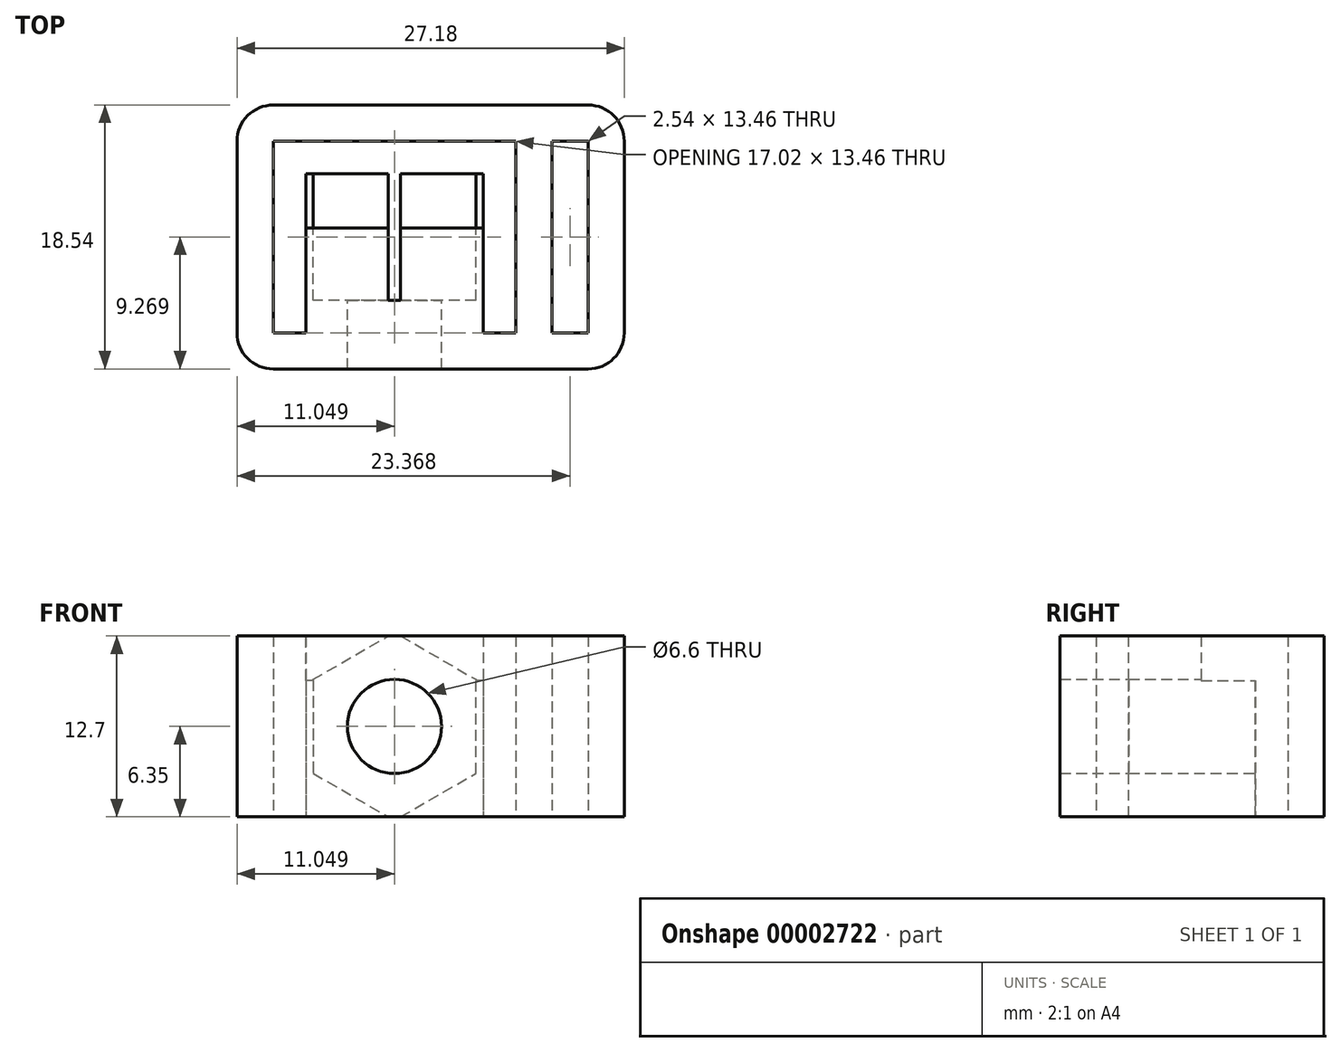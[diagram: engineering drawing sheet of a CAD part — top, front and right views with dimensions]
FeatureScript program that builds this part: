
annotation { "Feature Type Name" : "Feature", "Feature Type Description" : "" }
export const myFeature = defineFeature(function(context is Context, id is Id, definition is map)
    precondition{}
    {
        {
            var Q0;
            Q0=qCreatedBy(makeId("Top.planeOp"),FACE);
            var sketch = newSketch(context, id + "F0", { "sketchPlane" : qUnion([Q0])});
            skLineSegment(sketch, "E0", {"start": v(0, 0) * mm, "end": v(17.02, 0) * mm});
            skLineSegment(sketch, "E1", {"start": v(17.02, 0) * mm, "end": v(17.02, -13.46) * mm});
            skLineSegment(sketch, "E2", {"start": v(17.02, -13.46) * mm, "end": v(14.73, -13.46) * mm});
            skLineSegment(sketch, "E3", {"start": v(14.73, -13.46) * mm, "end": v(14.73, -2.29) * mm});
            skLineSegment(sketch, "E4", {"start": v(14.73, -2.29) * mm, "end": v(2.29, -2.29) * mm});
            skLineSegment(sketch, "E5", {"start": v(2.29, -2.29) * mm, "end": v(2.29, -13.46) * mm});
            skLineSegment(sketch, "E6", {"start": v(2.29, -13.46) * mm, "end": v(0, -13.46) * mm});
            skLineSegment(sketch, "E7", {"start": v(0, -13.46) * mm, "end": v(0, 0) * mm});
            skSolve(sketch);
        }
        {
            var Q0;
            Q0=qCreatedBy(makeId("Top.planeOp"),FACE);
            var sketch = newSketch(context, id + "F1", { "sketchPlane" : qUnion([Q0])});
            skLineSegment(sketch, "E8.0", {"start": v(0, 2.54) * mm, "end": v(17.02, 2.54) * mm});
            skLineSegment(sketch, "E9.0", {"start": v(-2.54, -13.46) * mm, "end": v(-2.54, 0) * mm});
            skLineSegment(sketch, "E10.0", {"start": v(19.56, 0) * mm, "end": v(19.56, -13.46) * mm});
            skArc(sketch, "E11", {"start": v(19.56, 0) * mm, "mid": v(18.81, 1.8) * mm, "end": v(17.02, 2.54) * mm});
            skArc(sketch, "E12", {"start": v(0, 2.54) * mm, "mid": v(-1.8, 1.8) * mm, "end": v(-2.54, 0) * mm});
            skLineSegment(sketch, "E13.0", {"start": v(17.02, -16) * mm, "end": v(0, -16) * mm});
            skArc(sketch, "E14", {"start": v(17.02, -16) * mm, "mid": v(18.81, -15.26) * mm, "end": v(19.56, -13.46) * mm});
            skArc(sketch, "E15", {"start": v(-2.54, -13.46) * mm, "mid": v(-1.8, -15.26) * mm, "end": v(0, -16) * mm});
            skSolve(sketch);
        }
        {
            var Q0;
            Q0=qCreatedBy(makeId("Top.planeOp"),FACE);
            var sketch = newSketch(context, id + "F2", { "sketchPlane" : qUnion([Q0])});
            skLineSegment(sketch, "E16", {"start": v(19.56, 0) * mm, "end": v(22.1, 0) * mm});
            skLineSegment(sketch, "E17", {"start": v(22.1, 0) * mm, "end": v(22.1, -13.46) * mm});
            skLineSegment(sketch, "E18", {"start": v(22.1, -13.46) * mm, "end": v(19.56, -13.46) * mm});
            skLineSegment(sketch, "E19", {"start": v(19.56, -13.46) * mm, "end": v(19.56, 0) * mm});
            skSolve(sketch);
        }
        {
            var Q0;
            Q0=qCreatedBy(makeId("Top.planeOp"),FACE);
            var sketch = newSketch(context, id + "F3", { "sketchPlane" : qUnion([Q0])});
            skLineSegment(sketch, "E20", {"start": v(17.02, -16) * mm, "end": v(22.1, -16) * mm});
            skLineSegment(sketch, "E21", {"start": v(24.64, -13.46) * mm, "end": v(24.64, 0) * mm});
            skLineSegment(sketch, "E22", {"start": v(22.1, 2.54) * mm, "end": v(17.02, 2.54) * mm});
            skLineSegment(sketch, "E23", {"start": v(17.02, 2.54) * mm, "end": v(17.02, -16) * mm});
            skPoint(sketch, "E24.visualSharp", {"position": v(24.64, -16) * mm});
            skArc(sketch, "E24.filletArc", {"start": v(22.1, -16) * mm, "mid": v(23.9, -15.26) * mm, "end": v(24.64, -13.46) * mm});
            skPoint(sketch, "E25.visualSharp", {"position": v(24.64, 2.54) * mm});
            skArc(sketch, "E25.filletArc", {"start": v(24.64, 0) * mm, "mid": v(23.9, 1.8) * mm, "end": v(22.1, 2.54) * mm});
            skSolve(sketch);
        }
        {
            var Q0;
            Q0=makeQuery(id+"F1.imprint","IMPRINT",FACE,{"disambiguationData":[TD([[makeQuery(id+"F1.imprint","IMPRINT",EDGE,{"derivedFrom":sQuery(id+"F1.wireOp",EDGE,"E8.0")}),-1.0]])]});
            extrude(context, id + "F4", {"entities" : qUnion([Q0]), "depth" : 12.7 * mm});
        }
        {
            var Q0;
            Q0=makeQuery(id+"F0.imprint","IMPRINT",FACE,{"disambiguationData":[TD([[makeQuery(id+"F0.imprint","IMPRINT",EDGE,{"derivedFrom":sQuery(id+"F0.wireOp",EDGE,"E0")}),-1.0]])]});
            var Q1;
            Q1=makeQuery(id+"F2.imprint","IMPRINT",FACE,{"disambiguationData":[TD([[makeQuery(id+"F2.imprint","IMPRINT",EDGE,{"derivedFrom":sQuery(id+"F2.wireOp",EDGE,"E16")}),-1.0]])]});
            extrude(context, id + "F5", {"entities" : qUnion([Q0, Q1]), "operationType" : NewBodyOperationType.REMOVE, "depth" : 12.7 * mm});
        }
        {
            var Q0;
            Q0=makeQuery(id+"F3.imprint","IMPRINT",FACE,{"disambiguationData":[TD([[makeQuery(id+"F3.imprint","IMPRINT",EDGE,{"derivedFrom":sQuery(id+"F3.wireOp",EDGE,"E20")}),1.0]])]});
            extrude(context, id + "F6", {"entities" : qUnion([Q0]), "operationType" : NewBodyOperationType.ADD, "depth" : 12.7 * mm});
        }
        {
            var Q0;
            Q0=makeQuery(id+"F2.imprint","IMPRINT",FACE,{"disambiguationData":[TD([[makeQuery(id+"F2.imprint","IMPRINT",EDGE,{"derivedFrom":sQuery(id+"F2.wireOp",EDGE,"E16")}),-1.0]])]});
            extrude(context, id + "F7", {"entities" : qUnion([Q0]), "operationType" : NewBodyOperationType.REMOVE, "depth" : 12.7 * mm});
        }
        {
            var Q0;
            Q0=makeQuery(id+"F5.boolean.opBoolean","COPY",FACE,{"derivedFrom":makeQuery(id+"F5.opExtrude","SWEPT_FACE",FACE,{"disambiguationData":[OSD([sQuery(id+"F0.wireOp",EDGE,"E4")])]})});
            var sketch = newSketch(context, id + "F8", { "sketchPlane" : qUnion([Q0])});
            skLineSegment(sketch, "E26", {"start": v(-2.29, 12.7) * mm, "end": v(-14.73, 0) * mm});
            skCircle(sketch, "E27.cCircle", {"center": v(-8.5, 6.35) * mm, "radius": 5.71 * mm, "construction": true});
            skLineSegment(sketch, "E27.0", {"start": v(-14.22, 3.05) * mm, "end": v(-14.22, 9.65) * mm});
            skLineSegment(sketch, "E27.1", {"start": v(-14.22, 9.65) * mm, "end": v(-8.5, 12.95) * mm});
            skLineSegment(sketch, "E27.2", {"start": v(-8.5, 12.95) * mm, "end": v(-2.8, 9.65) * mm});
            skLineSegment(sketch, "E27.3", {"start": v(-2.8, 9.65) * mm, "end": v(-2.8, 3.05) * mm});
            skLineSegment(sketch, "E27.4", {"start": v(-2.8, 3.05) * mm, "end": v(-8.5, -0.25) * mm});
            skLineSegment(sketch, "E27.5", {"start": v(-8.5, -0.25) * mm, "end": v(-14.22, 3.05) * mm});
            skPoint(sketch, "E27.0.midPoint", {"position": v(-14.22, 6.35) * mm});
            skSolve(sketch);
        }
        {
            var Q0;
            {var subQ2=sQuery(id+"F8.wireOp",EDGE,"E27.2");var subQ4=sQuery(id+"F8.wireOp",EDGE,"E27.1");var subQ7=makeQuery(id+"F8.imprint","INTERSECT",VERTEX,{"derivedFrom":[subQ4,subQ2]});var subQ9=sQuery(id+"F8.wireOp",EDGE,"E27.5");var subQ11=sQuery(id+"F8.wireOp",EDGE,"E27.4");var subQ14=makeQuery(id+"F8.imprint","INTERSECT",VERTEX,{"derivedFrom":[subQ11,subQ9]});var subQ17=sQuery(id+"F8.wireOp",EDGE,"E27.0");var subQ20=sQuery(id+"F8.wireOp",EDGE,"E27.3");Q0=qUnion([makeQuery(id+"F8.imprint","IMPRINT",FACE,{"disambiguationData":[TD([[makeQuery(id+"F8.imprint","IMPRINT",EDGE,{"disambiguationData":[TD([[subQ7,1.0]])],"derivedFrom":subQ4}),-1.0]])]}),makeQuery(id+"F8.imprint","IMPRINT",FACE,{"disambiguationData":[TD([[makeQuery(id+"F8.imprint","IMPRINT",EDGE,{"disambiguationData":[TD([[subQ14,1.0]])],"derivedFrom":subQ11}),-1.0]])]}),makeQuery(id+"F8.imprint","IMPRINT",FACE,{"disambiguationData":[TD([[makeQuery(id+"F8.imprint","IMPRINT",EDGE,{"derivedFrom":subQ17}),-1.0]])]}),makeQuery(id+"F8.imprint","IMPRINT",FACE,{"disambiguationData":[TD([[makeQuery(id+"F8.imprint","IMPRINT",EDGE,{"derivedFrom":subQ20}),-1.0]])]})]);}
            extrude(context, id + "F9", {"entities" : qUnion([Q0]), "operationType" : NewBodyOperationType.REMOVE, "oppositeDirection" : true, "depth" : 8.9 * mm});
        }
        {
            var Q0;
            Q0=makeQuery(id+"F9.boolean.opBoolean","SPLIT",FACE,{"disambiguationData":[TD([makeQuery(id+"F5.boolean.opBoolean","COPY",FACE,{"derivedFrom":makeQuery(id+"F5.opExtrude","SWEPT_FACE",FACE,{"disambiguationData":[OSD([sQuery(id+"F0.wireOp",EDGE,"E3")])]})})])],"derivedFrom":makeQuery(id+"F5.boolean.opBoolean","COPY",FACE,{"derivedFrom":makeQuery(id+"F5.opExtrude","SWEPT_FACE",FACE,{"disambiguationData":[OSD([sQuery(id+"F0.wireOp",EDGE,"E4")])]})})});
            var sketch = newSketch(context, id + "F10", { "sketchPlane" : qUnion([Q0])});
            skLineSegment(sketch, "E28.bottom", {"start": v(-14.73, 12.7) * mm, "end": v(-2.2, 12.7) * mm});
            skLineSegment(sketch, "E28.top", {"start": v(-14.73, 9.58) * mm, "end": v(-2.2, 9.58) * mm});
            skLineSegment(sketch, "E28.left", {"start": v(-14.73, 12.7) * mm, "end": v(-14.73, 9.58) * mm});
            skLineSegment(sketch, "E28.right", {"start": v(-2.2, 12.7) * mm, "end": v(-2.2, 9.58) * mm});
            skSolve(sketch);
        }
        {
            var Q0;
            {var subQ6=sQuery(id+"F10.wireOp",EDGE,"E28.right");var subQ9=sQuery(id+"F10.wireOp",EDGE,"E28.left");Q0=qUnion([makeQuery(id+"F10.imprint","IMPRINT",FACE,{"disambiguationData":[TD([[makeQuery(id+"F10.imprint","IMPRINT",EDGE,{"derivedFrom":subQ6}),-1.0]])]}),makeQuery(id+"F10.imprint","IMPRINT",FACE,{"disambiguationData":[TD([[makeQuery(id+"F10.imprint","IMPRINT",EDGE,{"derivedFrom":subQ9}),1.0]])]})]);}
            extrude(context, id + "F11", {"entities" : qUnion([Q0]), "operationType" : NewBodyOperationType.REMOVE, "oppositeDirection" : true, "depth" : 3.8 * mm});
        }
        {
            var Q0;
            {var subQ2=sQuery(id+"F8.wireOp",EDGE,"E27.2");var subQ4=sQuery(id+"F8.wireOp",EDGE,"E27.1");var subQ7=makeQuery(id+"F8.imprint","INTERSECT",VERTEX,{"derivedFrom":[subQ4,subQ2]});var subQ9=sQuery(id+"F8.wireOp",EDGE,"E27.5");var subQ11=sQuery(id+"F8.wireOp",EDGE,"E27.4");var subQ14=makeQuery(id+"F8.imprint","INTERSECT",VERTEX,{"derivedFrom":[subQ11,subQ9]});var subQ17=sQuery(id+"F8.wireOp",EDGE,"E27.0");var subQ20=sQuery(id+"F8.wireOp",EDGE,"E27.3");Q0=qUnion([makeQuery(id+"F8.imprint","IMPRINT",FACE,{"disambiguationData":[TD([[makeQuery(id+"F8.imprint","IMPRINT",EDGE,{"disambiguationData":[TD([[subQ7,1.0]])],"derivedFrom":subQ4}),-1.0]])]}),makeQuery(id+"F8.imprint","IMPRINT",FACE,{"disambiguationData":[TD([[makeQuery(id+"F8.imprint","IMPRINT",EDGE,{"disambiguationData":[TD([[subQ14,1.0]])],"derivedFrom":subQ11}),-1.0]])]}),makeQuery(id+"F8.imprint","IMPRINT",FACE,{"disambiguationData":[TD([[makeQuery(id+"F8.imprint","IMPRINT",EDGE,{"derivedFrom":subQ17}),-1.0]])]}),makeQuery(id+"F8.imprint","IMPRINT",FACE,{"disambiguationData":[TD([[makeQuery(id+"F8.imprint","IMPRINT",EDGE,{"derivedFrom":subQ20}),-1.0]])]})]);}
            var sketch = newSketch(context, id + "F12", { "sketchPlane" : qUnion([Q0])});
            skCircle(sketch, "E29", {"center": v(-8.5, 6.35) * mm, "radius": 3.3 * mm});
            skSolve(sketch);
        }
        {
            var Q0;
            {var subQ0=sQuery(id+"F8.wireOp",EDGE,"E26");var subQ1=makeQuery(id+"F8.imprint","IMPRINT",EDGE,{"disambiguationData":[TD([[makeQuery(id+"F8.imprint","INTERSECT",VERTEX,{"derivedFrom":[subQ0,sQuery(id+"F8.wireOp",EDGE,"E27.2")]}),-1.0]])],"derivedFrom":subQ0});var subQ2=sQuery(id+"F12.wireOp",EDGE,"E29");var subQ4=makeQuery(id+"F12.imprint","INTERSECT",VERTEX,{"disambiguationData":[OD(0.0)],"derivedFrom":[subQ1,subQ2]});Q0=qUnion([makeQuery(id+"F12.imprint","IMPRINT",FACE,{"disambiguationData":[TD([[makeQuery(id+"F12.imprint","IMPRINT",EDGE,{"disambiguationData":[TD([[subQ4,-1.0]])],"derivedFrom":subQ2}),1.0]])]}),makeQuery(id+"F12.imprint","IMPRINT",FACE,{"disambiguationData":[TD([[makeQuery(id+"F12.imprint","IMPRINT",EDGE,{"disambiguationData":[TD([[subQ4,1.0]])],"derivedFrom":subQ2}),1.0]])]})]);}
            extrude(context, id + "F13", {"entities" : qUnion([Q0]), "operationType" : NewBodyOperationType.REMOVE, "oppositeDirection" : true, "depth" : 25.4 * mm});
        }
    });
